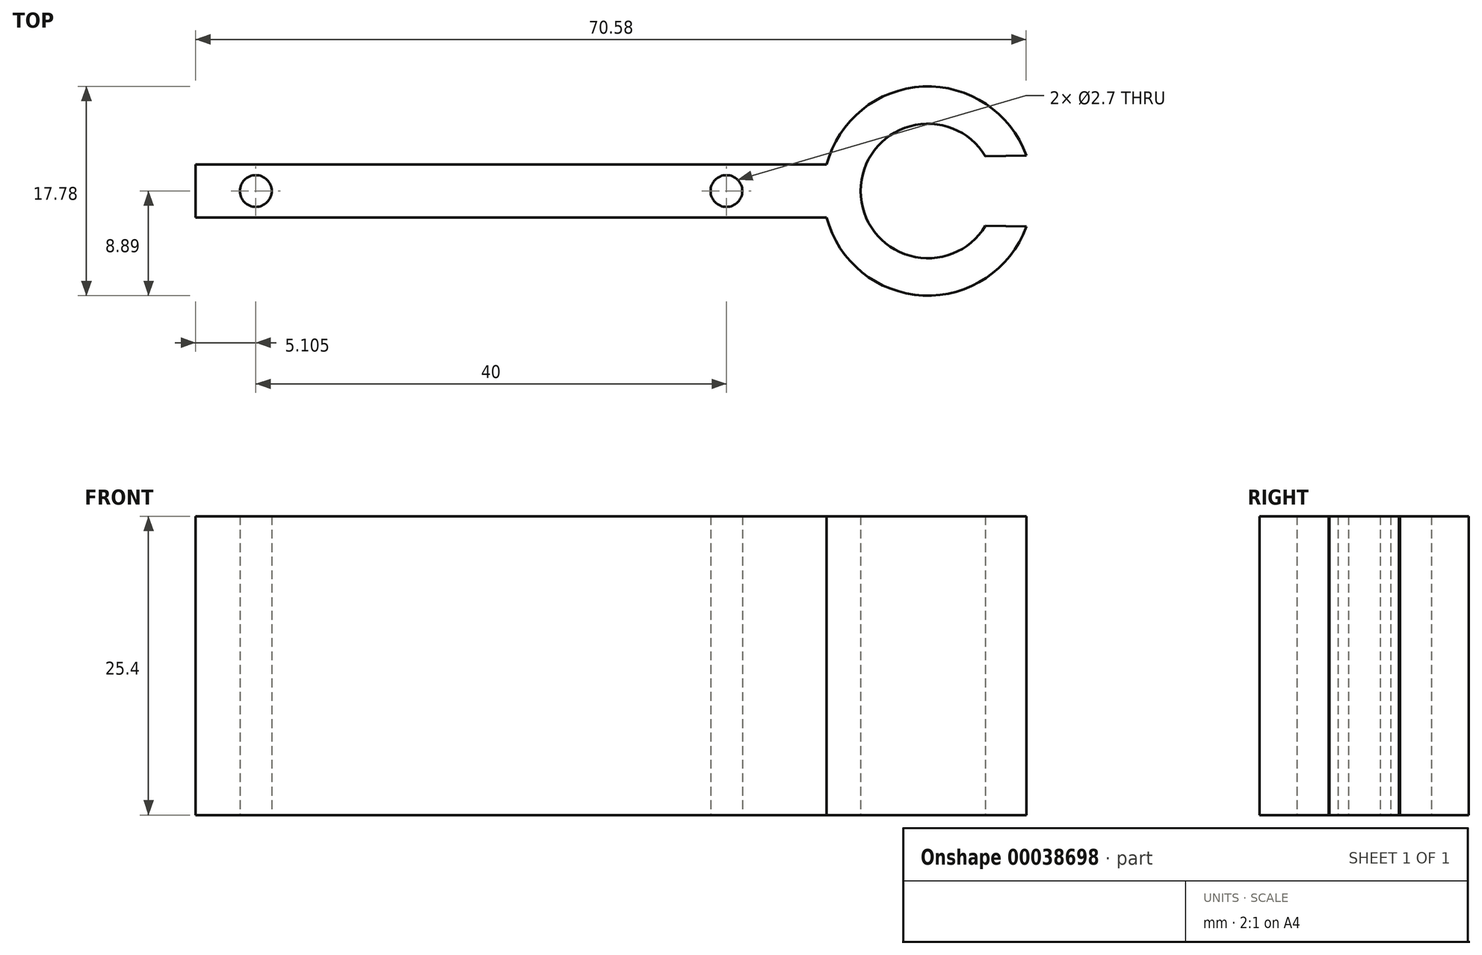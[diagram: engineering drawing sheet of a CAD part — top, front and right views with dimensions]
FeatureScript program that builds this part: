
annotation { "Feature Type Name" : "Feature", "Feature Type Description" : "" }
export const myFeature = defineFeature(function(context is Context, id is Id, definition is map)
    precondition{}
    {
        {
            var Q0;
            Q0=qCreatedBy(makeId("Top.planeOp"),FACE);
            var sketch = newSketch(context, id + "F0", { "sketchPlane" : qUnion([Q0])});
            skLineSegment(sketch, "E0.rect.right", {"start": v(-34.93, -2.24) * mm, "end": v(-34.93, 2.35) * mm});
            skPoint(sketch, "E0.rect.middle", {"position": v(0, 0) * mm});
            skArc(sketch, "E1", {"start": v(32.2, 2.95) * mm, "mid": v(21.59, 0) * mm, "end": v(32.2, -2.95) * mm});
            skCircle(sketch, "E2", {"center": v(-29.82, 0) * mm, "radius": 1.35 * mm});
            skCircle(sketch, "E3", {"center": v(10.18, 0) * mm, "radius": 1.35 * mm});
            skPoint(sketch, "E4.visualSharp", {"position": v(-34.93, 8.7) * mm});
            skPoint(sketch, "E5.visualSharp", {"position": v(-34.93, -8.7) * mm});
            skPoint(sketch, "E6.visualSharp", {"position": v(34.93, -8.7) * mm});
            skPoint(sketch, "E7.visualSharp", {"position": v(34.93, 8.7) * mm});
            skLineSegment(sketch, "E8", {"start": v(-34.93, -2.24) * mm, "end": v(18.7, -2.24) * mm});
            skLineSegment(sketch, "E9", {"start": v(-34.93, 2.24) * mm, "end": v(18.7, 2.24) * mm});
            skArc(sketch, "E10.0", {"start": v(18.7, -2.24) * mm, "mid": v(26.9, -8.88) * mm, "end": v(35.66, -3.03) * mm});
            skLineSegment(sketch, "E11.0", {"start": v(32.2, -2.95) * mm, "end": v(35.69, -3.03) * mm});
            skLineSegment(sketch, "E12.0", {"start": v(32.2, 2.95) * mm, "end": v(35.66, 3.03) * mm});
            skArc(sketch, "E13.trimOffspring", {"start": v(35.66, 3.03) * mm, "mid": v(26.9, 8.88) * mm, "end": v(18.7, 2.24) * mm});
            skPoint(sketch, "E14.start.orphan", {"position": v(33.02, 0) * mm});
            skSolve(sketch);
        }
        {
            var Q0;
            Q0 = qSketchRegion(id + "F0", true);
            extrude(context, id + "F1", {"entities" : qUnion([Q0]), "depth" : 25.4 * mm});
        }
    });
